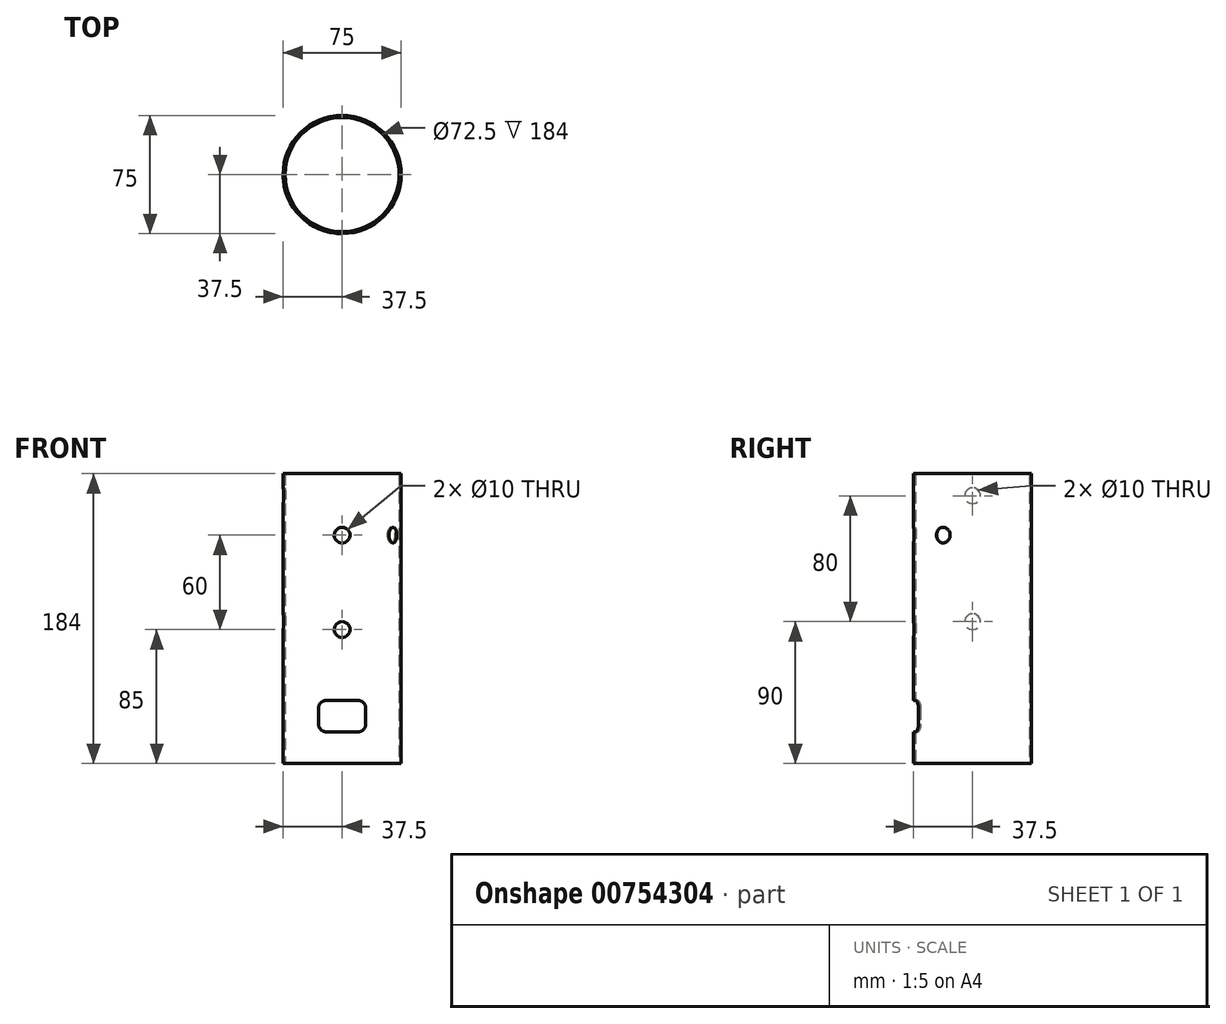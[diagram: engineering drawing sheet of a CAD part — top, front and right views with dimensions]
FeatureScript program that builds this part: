
annotation { "Feature Type Name" : "Feature", "Feature Type Description" : "" }
export const myFeature = defineFeature(function(context is Context, id is Id, definition is map)
    precondition{}
    {
        {
            var Q0;
            Q0=qCreatedBy(makeId("Top.planeOp"),FACE);
            var sketch = newSketch(context, id + "F0", { "sketchPlane" : qUnion([Q0])});
            skCircle(sketch, "E0", {"center": v(0, 0) * mm, "radius": 36.25 * mm});
            skCircle(sketch, "E1", {"center": v(0, 0) * mm, "radius": 37.5 * mm});
            skLineSegment(sketch, "E2", {"start": v(0, 0) * mm, "end": v(26.96, -46.69) * mm, "construction": true});
            skSolve(sketch);
        }
        {
            var Q0;
            Q0=makeQuery(id+"F0.imprint","IMPRINT",FACE,{"disambiguationData":[TD([[makeQuery(id+"F0.imprint","IMPRINT",EDGE,{"derivedFrom":sQuery(id+"F0.wireOp",EDGE,"E0")}),-1.0]])]});
            extrude(context, id + "F1", {"entities" : qUnion([Q0]), "depth" : 184 * mm, "offsetDistance" : 25 * mm});
        }
        {
            var Q0;
            Q0=qCreatedBy(makeId("Right.planeOp"),FACE);
            var sketch = newSketch(context, id + "F2", { "sketchPlane" : qUnion([Q0])});
            skLineSegment(sketch, "E3", {"start": v(0, 0) * mm, "end": v(0, 170) * mm, "construction": true});
            skCircle(sketch, "E4", {"center": v(0, 170) * mm, "radius": 5 * mm});
            skSolve(sketch);
        }
        {
            var Q0;
            Q0 = qSketchRegion(id + "F2", true);
            extrude(context, id + "F3", {"entities" : qUnion([Q0]), "operationType" : NewBodyOperationType.REMOVE, "oppositeDirection" : true, "depth" : 50 * mm, "offsetDistance" : 25 * mm});
        }
        {
            var Q0;
            Q0=qCreatedBy(makeId("Front.planeOp"),FACE);
            var sketch = newSketch(context, id + "F4", { "sketchPlane" : qUnion([Q0])});
            skLineSegment(sketch, "E5", {"start": v(0, 0) * mm, "end": v(0, 85) * mm, "construction": true});
            skLineSegment(sketch, "E6", {"start": v(0, 85) * mm, "end": v(0, 145) * mm, "construction": true});
            skCircle(sketch, "E7", {"center": v(0, 85) * mm, "radius": 5 * mm});
            skCircle(sketch, "E8", {"center": v(0, 145) * mm, "radius": 5 * mm});
            skSolve(sketch);
        }
        {
            var Q0;
            Q0 = qSketchRegion(id + "F4", true);
            extrude(context, id + "F5", {"entities" : qUnion([Q0]), "operationType" : NewBodyOperationType.REMOVE, "depth" : 70 * mm, "offsetDistance" : 25 * mm, "hasSecondDirection" : true, "secondDirectionOppositeDirection" : true, "secondDirectionDepth" : 25 * mm});
        }
        {
            var Q0;
            Q0=qCreatedBy(makeId("Front.planeOp"),FACE);
            var sketch = newSketch(context, id + "F6", { "sketchPlane" : qUnion([Q0])});
            skLineSegment(sketch, "E9", {"start": v(0, 0) * mm, "end": v(0, 30) * mm, "construction": true});
            skLineSegment(sketch, "E10.bottom", {"start": v(10, 20) * mm, "end": v(-10, 20) * mm});
            skLineSegment(sketch, "E10.top", {"start": v(10, 40) * mm, "end": v(-10, 40) * mm});
            skLineSegment(sketch, "E10.left", {"start": v(15, 25) * mm, "end": v(15, 35) * mm});
            skLineSegment(sketch, "E10.right", {"start": v(-15, 25) * mm, "end": v(-15, 35) * mm});
            skPoint(sketch, "E10.middle", {"position": v(0, 30) * mm});
            skPoint(sketch, "E11.visualSharp", {"position": v(-15, 40) * mm});
            skArc(sketch, "E11.filletArc", {"start": v(-10, 40) * mm, "mid": v(-13.54, 38.54) * mm, "end": v(-15, 35) * mm});
            skPoint(sketch, "E12.visualSharp", {"position": v(15, 40) * mm});
            skArc(sketch, "E12.filletArc", {"start": v(15, 35) * mm, "mid": v(13.54, 38.54) * mm, "end": v(10, 40) * mm});
            skPoint(sketch, "E13.visualSharp", {"position": v(15, 20) * mm});
            skArc(sketch, "E13.filletArc", {"start": v(10, 20) * mm, "mid": v(13.54, 21.46) * mm, "end": v(15, 25) * mm});
            skPoint(sketch, "E14.visualSharp", {"position": v(-15, 20) * mm});
            skArc(sketch, "E14.filletArc", {"start": v(-15, 25) * mm, "mid": v(-13.54, 21.46) * mm, "end": v(-10, 20) * mm});
            skSolve(sketch);
        }
        {
            var Q0;
            Q0 = qSketchRegion(id + "F6", true);
            extrude(context, id + "F7", {"entities" : qUnion([Q0]), "operationType" : NewBodyOperationType.REMOVE, "depth" : 70 * mm, "offsetDistance" : 25 * mm});
        }
        {
            var Q0;
            Q0=qCreatedBy(makeId("Right.planeOp"),FACE);
            var sketch = newSketch(context, id + "F8", { "sketchPlane" : qUnion([Q0])});
            skLineSegment(sketch, "E15", {"start": v(0, 0) * mm, "end": v(0, 90) * mm, "construction": true});
            skCircle(sketch, "E16", {"center": v(0, 90) * mm, "radius": 5 * mm});
            skSolve(sketch);
        }
        {
            var Q0;
            Q0 = qSketchRegion(id + "F8", true);
            extrude(context, id + "F9", {"entities" : qUnion([Q0]), "operationType" : NewBodyOperationType.REMOVE, "oppositeDirection" : true, "depth" : 60 * mm, "offsetDistance" : 25 * mm});
        }
        {
            var Q0;
            Q0=qCreatedBy(makeId("Top.planeOp"),FACE);
            var sketch = newSketch(context, id + "F10", { "sketchPlane" : qUnion([Q0])});
            skLineSegment(sketch, "E17", {"start": v(0, 0) * mm, "end": v(-30, -51.96) * mm});
            skSolve(sketch);
        }
        {
            var Q0;
            Q0=sQuery(id+"F10.wireOp",EDGE,"E17");
            cPlane(context, id + "F11", {"entities" : qUnion([Q0]), "cplaneType" : CPlaneType.LINE_ANGLE, "offset" : 25 * mm, "angle" : 90 * degree, "width" : 150 * mm, "height" : 150 * mm});
        }
        {
            var Q0;
            Q0=qCreatedBy(id+"F11.planeOp",FACE);
            var sketch = newSketch(context, id + "F12", { "sketchPlane" : qUnion([Q0])});
            skLineSegment(sketch, "E18", {"start": v(0, 0) * mm, "end": v(0, 145) * mm, "construction": true});
            skCircle(sketch, "E19", {"center": v(0, 145) * mm, "radius": 5 * mm});
            skSolve(sketch);
        }
        {
            var Q0;
            Q0=makeQuery(id+"F12.imprint","IMPRINT",FACE,{"disambiguationData":[TD([[makeQuery(id+"F12.imprint","IMPRINT",EDGE,{"derivedFrom":sQuery(id+"F12.wireOp",EDGE,"E19")}),1.0]])]});
            var Q1;
            Q1=sQuery(id+"F12.wireOp",EDGE,"E19");
            extrude(context, id + "F13", {"entities" : qUnion([Q0]), "operationType" : NewBodyOperationType.REMOVE, "surfaceEntities" : qUnion([Q1]), "depth" : 100 * mm, "offsetDistance" : 25 * mm});
        }
    });
